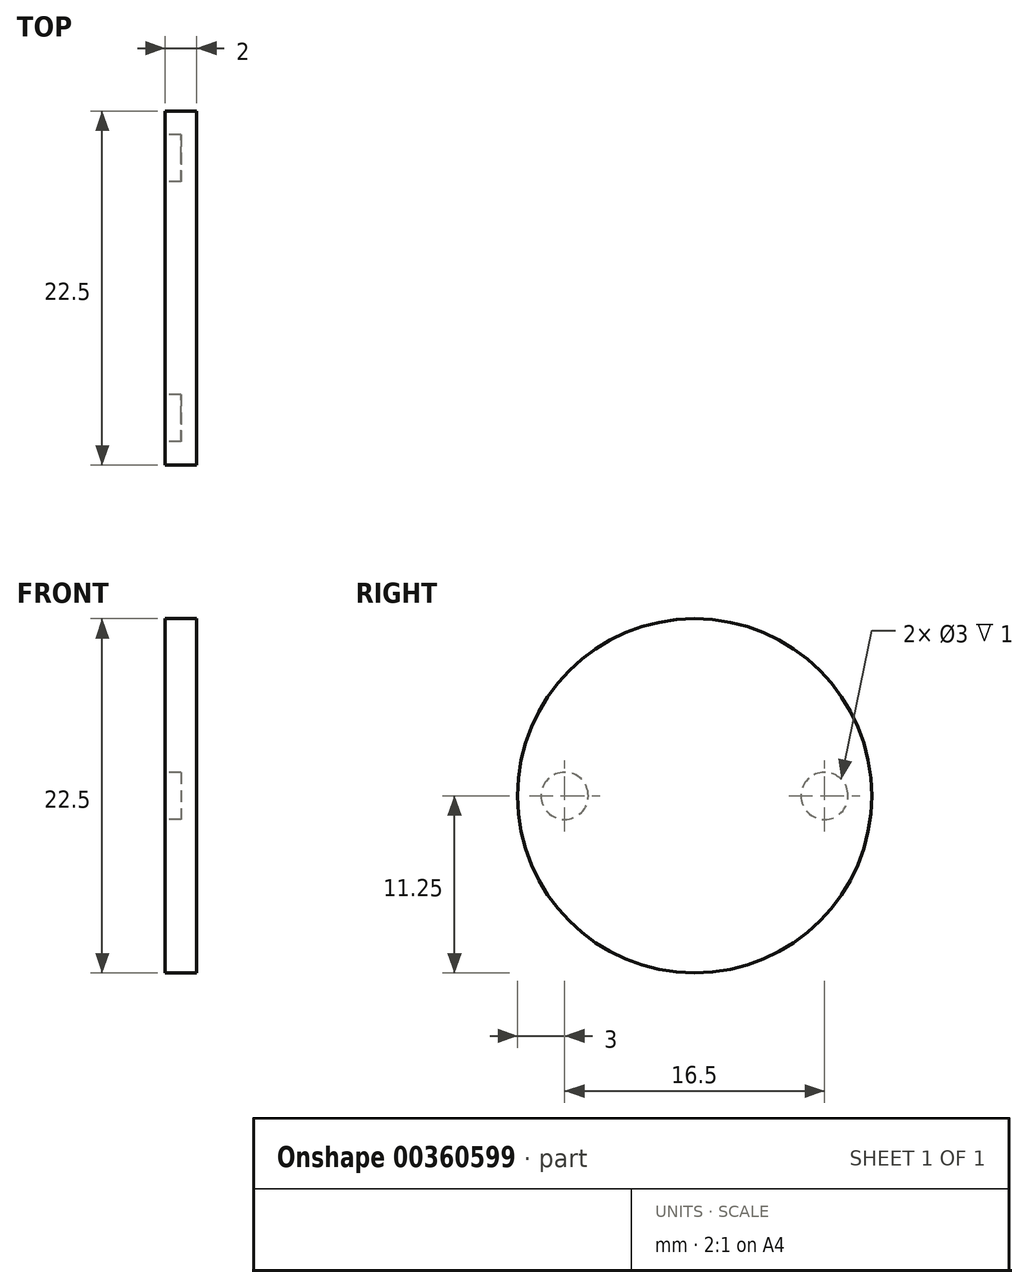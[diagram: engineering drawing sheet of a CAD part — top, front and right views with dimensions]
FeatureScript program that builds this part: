
annotation { "Feature Type Name" : "Feature", "Feature Type Description" : "" }
export const myFeature = defineFeature(function(context is Context, id is Id, definition is map)
    precondition{}
    {
        {
            var Q0;
            Q0=qCreatedBy(makeId("Right.planeOp"),FACE);
            var sketch = newSketch(context, id + "F0", { "sketchPlane" : qUnion([Q0])});
            skCircle(sketch, "E0", {"center": v(0, 0) * mm, "radius": 11.25 * mm});
            skSolve(sketch);
        }
        {
            var Q0;
            Q0 = qSketchRegion(id + "F0", true);
            extrude(context, id + "F1", {"entities" : qUnion([Q0]), "depth" : 2 * mm});
        }
        {
            var Q0;
            Q0=makeQuery(id+"F1.opExtrude","CAP_FACE",FACE,{"disambiguationData":[OSD([sQuery(id+"F0.wireOp",EDGE,"E0")])],"isStart":true});
            var sketch = newSketch(context, id + "F2", { "sketchPlane" : qUnion([Q0])});
            skLineSegment(sketch, "E1", {"start": v(-11.25, 0) * mm, "end": v(11.25, 0) * mm});
            skLineSegment(sketch, "E2", {"start": v(-11.25, 0) * mm, "end": v(-8.25, 0) * mm});
            skLineSegment(sketch, "E3", {"start": v(11.25, 0) * mm, "end": v(8.25, 0) * mm});
            skCircle(sketch, "E4", {"center": v(-8.25, 0) * mm, "radius": 1.5 * mm});
            skCircle(sketch, "E5", {"center": v(8.25, 0) * mm, "radius": 1.5 * mm});
            skSolve(sketch);
        }
        {
            var Q0;
            Q0 = qSketchRegion(id + "F2", true);
            extrude(context, id + "F3", {"entities" : qUnion([Q0]), "operationType" : NewBodyOperationType.REMOVE, "oppositeDirection" : true, "depth" : 1 * mm});
        }
    });
